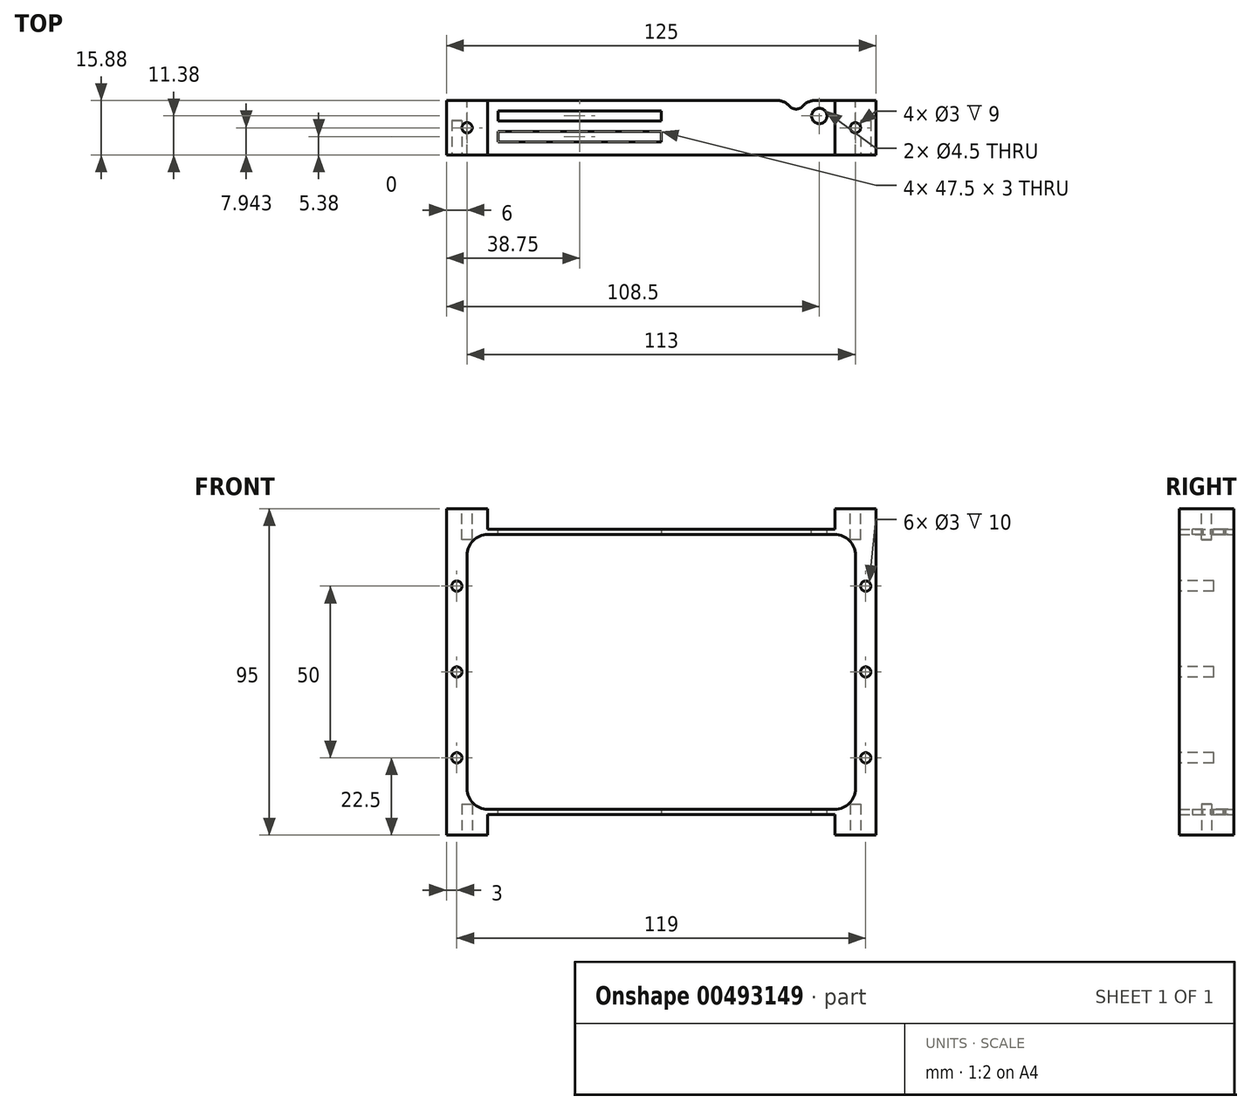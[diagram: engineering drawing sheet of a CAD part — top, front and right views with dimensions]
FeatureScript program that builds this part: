
annotation { "Feature Type Name" : "Feature", "Feature Type Description" : "" }
export const myFeature = defineFeature(function(context is Context, id is Id, definition is map)
    precondition{}
    {
        {
            var Q0;
            Q0=qCreatedBy(makeId("Front.planeOp"),FACE);
            var sketch = newSketch(context, id + "F0", { "sketchPlane" : qUnion([Q0])});
            skLineSegment(sketch, "E0.bottom", {"start": v(62.5, 47.5) * mm, "end": v(-62.5, 47.5) * mm, "construction": true});
            skLineSegment(sketch, "E0.top", {"start": v(62.5, -47.5) * mm, "end": v(-62.5, -47.5) * mm, "construction": true});
            skLineSegment(sketch, "E0.left", {"start": v(62.5, 47.5) * mm, "end": v(62.5, -47.5) * mm, "construction": true});
            skLineSegment(sketch, "E0.right", {"start": v(-62.5, 47.5) * mm, "end": v(-62.5, -47.5) * mm, "construction": true});
            skPoint(sketch, "E0.middle", {"position": v(0, 0) * mm});
            skLineSegment(sketch, "E1", {"start": v(-62.5, 47.5) * mm, "end": v(-50.5, 47.5) * mm});
            skLineSegment(sketch, "E2", {"start": v(62.5, 47.5) * mm, "end": v(50.5, 47.5) * mm});
            skLineSegment(sketch, "E3", {"start": v(50.5, 47.5) * mm, "end": v(50.5, 41.5) * mm});
            skLineSegment(sketch, "E4", {"start": v(50.5, 41.5) * mm, "end": v(-50.5, 41.5) * mm});
            skLineSegment(sketch, "E5", {"start": v(-50.5, 41.5) * mm, "end": v(-50.5, 47.5) * mm});
            skLineSegment(sketch, "E6", {"start": v(62.5, 47.5) * mm, "end": v(62.5, -47.5) * mm});
            skLineSegment(sketch, "E7", {"start": v(-62.5, -47.5) * mm, "end": v(-62.5, 47.5) * mm});
            skLineSegment(sketch, "E8", {"start": v(62.5, -47.5) * mm, "end": v(50.5, -47.5) * mm});
            skLineSegment(sketch, "E9", {"start": v(50.5, -47.5) * mm, "end": v(50.5, -41.5) * mm});
            skLineSegment(sketch, "E10", {"start": v(50.5, -41.5) * mm, "end": v(-50.5, -41.5) * mm});
            skLineSegment(sketch, "E11", {"start": v(-50.5, -41.5) * mm, "end": v(-50.5, -47.5) * mm});
            skLineSegment(sketch, "E12", {"start": v(-50.5, -47.5) * mm, "end": v(-62.5, -47.5) * mm});
            skLineSegment(sketch, "E13.bottom", {"start": v(56.5, 40) * mm, "end": v(-56.5, 40) * mm, "construction": true});
            skLineSegment(sketch, "E13.top", {"start": v(56.5, -40) * mm, "end": v(-56.5, -40) * mm, "construction": true});
            skLineSegment(sketch, "E13.left", {"start": v(56.5, 40) * mm, "end": v(56.5, -40) * mm, "construction": true});
            skLineSegment(sketch, "E13.right", {"start": v(-56.5, 40) * mm, "end": v(-56.5, -40) * mm, "construction": true});
            skLineSegment(sketch, "E14.bottom", {"start": v(56.5, 40) * mm, "end": v(-56.5, 40) * mm});
            skLineSegment(sketch, "E14.top", {"start": v(56.5, -40) * mm, "end": v(-56.5, -40) * mm});
            skLineSegment(sketch, "E14.left", {"start": v(56.5, 40) * mm, "end": v(56.5, -40) * mm});
            skLineSegment(sketch, "E14.right", {"start": v(-56.5, 40) * mm, "end": v(-56.5, -40) * mm});
            skSolve(sketch);
        }
        {
            var Q0;
            Q0 = qSketchRegion(id + "F0", true);
            extrude(context, id + "F1", {"entities" : qUnion([Q0]), "depth" : 15.88 * mm});
        }
        {
            var Q0;
            Q0=makeQuery(id+"F1.opExtrude","SWEPT_EDGE",EDGE,{"disambiguationData":[OSD([sQuery(id+"F0.wireOp",EDGE,"E14.bottom"),sQuery(id+"F0.wireOp",EDGE,"E14.left")])]});
            var Q1;
            Q1=makeQuery(id+"F1.opExtrude","SWEPT_EDGE",EDGE,{"disambiguationData":[OSD([sQuery(id+"F0.wireOp",EDGE,"E14.top"),sQuery(id+"F0.wireOp",EDGE,"E14.left")])]});
            var Q2;
            Q2=makeQuery(id+"F1.opExtrude","SWEPT_EDGE",EDGE,{"disambiguationData":[OSD([sQuery(id+"F0.wireOp",EDGE,"E14.top"),sQuery(id+"F0.wireOp",EDGE,"E14.right")])]});
            var Q3;
            Q3=makeQuery(id+"F1.opExtrude","SWEPT_EDGE",EDGE,{"disambiguationData":[OSD([sQuery(id+"F0.wireOp",EDGE,"E14.bottom"),sQuery(id+"F0.wireOp",EDGE,"E14.right")])]});
            fillet(context, id + "F2", {"entities" : qUnion([Q0, Q1, Q2, Q3]), "radius" : 6 * mm, "tangentPropagation" : true, "allowEdgeOverflow" : false});
        }
        {
            var Q0;
            Q0=makeQuery(id+"F1.opExtrude","SWEPT_FACE",FACE,{"disambiguationData":[OSD([sQuery(id+"F0.wireOp",EDGE,"E4")])]});
            var sketch = newSketch(context, id + "F3", { "sketchPlane" : qUnion([Q0])});
            skLineSegment(sketch, "E15.bottom", {"start": v(-47.5, -3) * mm, "end": v(41.5, -3) * mm});
            skLineSegment(sketch, "E15.top", {"start": v(-47.5, -6) * mm, "end": v(41.5, -6) * mm});
            skLineSegment(sketch, "E15.left", {"start": v(-47.5, -3) * mm, "end": v(-47.5, -6) * mm});
            skLineSegment(sketch, "E15.right", {"start": v(41.5, -3) * mm, "end": v(41.5, -6) * mm});
            skLineSegment(sketch, "E16.bottom", {"start": v(-47.5, -9) * mm, "end": v(47.5, -9) * mm});
            skLineSegment(sketch, "E16.top", {"start": v(-47.5, -12) * mm, "end": v(47.5, -12) * mm});
            skLineSegment(sketch, "E16.left", {"start": v(-47.5, -9) * mm, "end": v(-47.5, -12) * mm});
            skLineSegment(sketch, "E16.right", {"start": v(47.5, -9) * mm, "end": v(47.5, -12) * mm});
            skCircle(sketch, "E17", {"center": v(46, -4.5) * mm, "radius": 1.5 * mm});
            skSolve(sketch);
        }
        {
            var Q0;
            Q0 = qSketchRegion(id + "F3", true);
            extrude(context, id + "F4", {"entities" : qUnion([Q0]), "operationType" : NewBodyOperationType.REMOVE, "oppositeDirection" : true, "depth" : 132 * mm});
        }
        {
            var Q0;
            Q0=makeQuery(id+"F1.opExtrude","CAP_FACE",FACE,{"disambiguationData":[OSD([sQuery(id+"F0.wireOp",EDGE,"E1"),sQuery(id+"F0.wireOp",EDGE,"E2"),sQuery(id+"F0.wireOp",EDGE,"E3"),sQuery(id+"F0.wireOp",EDGE,"E4"),sQuery(id+"F0.wireOp",EDGE,"E5"),sQuery(id+"F0.wireOp",EDGE,"E6"),sQuery(id+"F0.wireOp",EDGE,"E7"),sQuery(id+"F0.wireOp",EDGE,"E8"),sQuery(id+"F0.wireOp",EDGE,"E9"),sQuery(id+"F0.wireOp",EDGE,"E10"),sQuery(id+"F0.wireOp",EDGE,"E11"),sQuery(id+"F0.wireOp",EDGE,"E12"),sQuery(id+"F0.wireOp",EDGE,"E14.bottom"),sQuery(id+"F0.wireOp",EDGE,"E14.top"),sQuery(id+"F0.wireOp",EDGE,"E14.left"),sQuery(id+"F0.wireOp",EDGE,"E14.right")])],"isStart":false});
            var sketch = newSketch(context, id + "F5", { "sketchPlane" : qUnion([Q0])});
            skLineSegment(sketch, "E18.bottom", {"start": v(-62.5, 32.98) * mm, "end": v(-56.5, 32.98) * mm, "construction": true});
            skLineSegment(sketch, "E18.top", {"start": v(-62.5, -31.1) * mm, "end": v(-56.5, -31.1) * mm, "construction": true});
            skLineSegment(sketch, "E18.left", {"start": v(-62.5, 32.98) * mm, "end": v(-62.5, -31.1) * mm, "construction": true});
            skLineSegment(sketch, "E18.right", {"start": v(-56.5, 32.98) * mm, "end": v(-56.5, -31.1) * mm, "construction": true});
            skLineSegment(sketch, "E19.bottom", {"start": v(56.5, 34) * mm, "end": v(62.5, 34) * mm, "construction": true});
            skLineSegment(sketch, "E19.top", {"start": v(56.5, -34) * mm, "end": v(62.5, -34) * mm, "construction": true});
            skLineSegment(sketch, "E19.left", {"start": v(56.5, 34) * mm, "end": v(56.5, -34) * mm, "construction": true});
            skLineSegment(sketch, "E19.right", {"start": v(62.5, 34) * mm, "end": v(62.5, -34) * mm, "construction": true});
            skLineSegment(sketch, "E20", {"start": v(-59.5, 32.98) * mm, "end": v(-59.5, -31.1) * mm, "construction": true});
            skLineSegment(sketch, "E21", {"start": v(-59.5, -31.1) * mm, "end": v(59.5, -34) * mm, "construction": true});
            skLineSegment(sketch, "E22", {"start": v(59.5, -34) * mm, "end": v(59.5, 34) * mm, "construction": true});
            skCircle(sketch, "E23", {"center": v(-59.5, 0) * mm, "radius": 1.5 * mm});
            skPoint(sketch, "E23.centerSnap0", {"position": v(-56.5, 0) * mm});
            skCircle(sketch, "E24", {"center": v(59.5, 0) * mm, "radius": 1.5 * mm});
            skCircle(sketch, "E25", {"center": v(59.5, -25) * mm, "radius": 1.5 * mm});
            skCircle(sketch, "E26", {"center": v(59.5, 25) * mm, "radius": 1.5 * mm});
            skCircle(sketch, "E27", {"center": v(-59.5, 25) * mm, "radius": 1.5 * mm});
            skCircle(sketch, "E28", {"center": v(-59.5, -25) * mm, "radius": 1.5 * mm});
            skSolve(sketch);
        }
        {
            var Q0;
            Q0 = qSketchRegion(id + "F5", true);
            extrude(context, id + "F6", {"entities" : qUnion([Q0]), "operationType" : NewBodyOperationType.REMOVE, "oppositeDirection" : true, "depth" : 10 * mm});
        }
        {
            var Q0;
            Q0=makeQuery(id+"F1.opExtrude","SWEPT_FACE",FACE,{"disambiguationData":[OSD([sQuery(id+"F0.wireOp",EDGE,"E4")])]});
            var sketch = newSketch(context, id + "F7", { "sketchPlane" : qUnion([Q0])});
            skLineSegment(sketch, "E29.bottom", {"start": v(0, 0) * mm, "end": v(42.94, 0) * mm});
            skLineSegment(sketch, "E29.top", {"start": v(0, -7.4) * mm, "end": v(42.94, -7.4) * mm});
            skLineSegment(sketch, "E29.left", {"start": v(0, 0) * mm, "end": v(0, -7.4) * mm});
            skLineSegment(sketch, "E29.right", {"start": v(42.94, 0) * mm, "end": v(42.94, -7.4) * mm});
            skLineSegment(sketch, "E30.bottom", {"start": v(0, -7.4) * mm, "end": v(49.14, -7.4) * mm});
            skLineSegment(sketch, "E30.top", {"start": v(0, -14.14) * mm, "end": v(49.14, -14.14) * mm});
            skLineSegment(sketch, "E30.left", {"start": v(0, -7.4) * mm, "end": v(0, -14.14) * mm});
            skLineSegment(sketch, "E30.right", {"start": v(49.14, -7.4) * mm, "end": v(49.14, -14.14) * mm});
            skSolve(sketch);
        }
        {
            var Q0;
            Q0 = qSketchRegion(id + "F7", true);
            extrude(context, id + "F8", {"entities" : qUnion([Q0]), "operationType" : NewBodyOperationType.ADD, "oppositeDirection" : true, "depth" : 1.5 * mm});
        }
        {
            var Q0;
            Q0=makeQuery(id+"F1.opExtrude","SWEPT_FACE",FACE,{"disambiguationData":[OSD([sQuery(id+"F0.wireOp",EDGE,"E10")])]});
            var sketch = newSketch(context, id + "F9", { "sketchPlane" : qUnion([Q0])});
            skLineSegment(sketch, "E31.bottom", {"start": v(0, 15.88) * mm, "end": v(49.01, 15.88) * mm});
            skLineSegment(sketch, "E31.top", {"start": v(0, 7.24) * mm, "end": v(49.01, 7.24) * mm});
            skLineSegment(sketch, "E31.left", {"start": v(0, 15.88) * mm, "end": v(0, 7.24) * mm});
            skLineSegment(sketch, "E31.right", {"start": v(49.01, 15.88) * mm, "end": v(49.01, 7.24) * mm});
            skLineSegment(sketch, "E32.bottom", {"start": v(0, 0) * mm, "end": v(42.8, 0) * mm});
            skLineSegment(sketch, "E32.top", {"start": v(0, 7.24) * mm, "end": v(42.8, 7.24) * mm});
            skLineSegment(sketch, "E32.left", {"start": v(0, 0) * mm, "end": v(0, 7.24) * mm});
            skLineSegment(sketch, "E32.right", {"start": v(42.8, 0) * mm, "end": v(42.8, 7.24) * mm});
            skSolve(sketch);
        }
        {
            var Q0;
            Q0 = qSketchRegion(id + "F9", true);
            extrude(context, id + "F10", {"entities" : qUnion([Q0]), "operationType" : NewBodyOperationType.ADD, "oppositeDirection" : true, "depth" : 1.5 * mm});
        }
        {
            var Q0;
            Q0=makeQuery(id+"F8.boolean.opBoolean","MERGE",FACE,{"derivedFrom":[makeQuery(id+"F1.opExtrude","SWEPT_FACE",FACE,{"disambiguationData":[OSD([sQuery(id+"F0.wireOp",EDGE,"E4")])]}),makeQuery(id+"F8.opExtrude","CAP_FACE",FACE,{"disambiguationData":[OSD([sQuery(id+"F7.wireOp",EDGE,"E29.bottom"),sQuery(id+"F7.wireOp",EDGE,"E29.left"),sQuery(id+"F7.wireOp",EDGE,"E29.right"),sQuery(id+"F7.wireOp",EDGE,"E30.bottom"),sQuery(id+"F7.wireOp",EDGE,"E30.top"),sQuery(id+"F7.wireOp",EDGE,"E30.left"),sQuery(id+"F7.wireOp",EDGE,"E30.right")])],"isStart":true})]});
            var sketch = newSketch(context, id + "F11", { "sketchPlane" : qUnion([Q0])});
            skCircle(sketch, "E33", {"center": v(39.25, 0) * mm, "radius": 2.5 * mm});
            skSolve(sketch);
        }
        {
            var Q0;
            Q0 = qSketchRegion(id + "F11", true);
            extrude(context, id + "F12", {"entities" : qUnion([Q0]), "operationType" : NewBodyOperationType.REMOVE, "oppositeDirection" : true, "depth" : 92 * mm});
        }
        {
            var Q0;
            Q0=makeQuery(id+"F8.boolean.opBoolean","MERGE",FACE,{"derivedFrom":[makeQuery(id+"F1.opExtrude","SWEPT_FACE",FACE,{"disambiguationData":[OSD([sQuery(id+"F0.wireOp",EDGE,"E4")])]}),makeQuery(id+"F8.opExtrude","CAP_FACE",FACE,{"disambiguationData":[OSD([sQuery(id+"F7.wireOp",EDGE,"E29.bottom"),sQuery(id+"F7.wireOp",EDGE,"E29.left"),sQuery(id+"F7.wireOp",EDGE,"E29.right"),sQuery(id+"F7.wireOp",EDGE,"E30.bottom"),sQuery(id+"F7.wireOp",EDGE,"E30.top"),sQuery(id+"F7.wireOp",EDGE,"E30.left"),sQuery(id+"F7.wireOp",EDGE,"E30.right")])],"isStart":true})]});
            var sketch = newSketch(context, id + "F13", { "sketchPlane" : qUnion([Q0])});
            skCircle(sketch, "E34", {"center": v(46, -4.5) * mm, "radius": 2.25 * mm});
            skSolve(sketch);
        }
        {
            var Q0;
            Q0 = qSketchRegion(id + "F13", true);
            extrude(context, id + "F14", {"entities" : qUnion([Q0]), "operationType" : NewBodyOperationType.REMOVE, "oppositeDirection" : true, "depth" : 200 * mm});
        }
        {
            var Q0;
            Q0=makeQuery(id+"F12.boolean.opBoolean","INTERSECT",EDGE,{"disambiguationData":[OD(2.0)],"derivedFrom":[makeQuery(id+"F1.opExtrude","CAP_FACE",FACE,{"disambiguationData":[OSD([sQuery(id+"F0.wireOp",EDGE,"E1"),sQuery(id+"F0.wireOp",EDGE,"E2"),sQuery(id+"F0.wireOp",EDGE,"E3"),sQuery(id+"F0.wireOp",EDGE,"E4"),sQuery(id+"F0.wireOp",EDGE,"E5"),sQuery(id+"F0.wireOp",EDGE,"E6"),sQuery(id+"F0.wireOp",EDGE,"E7"),sQuery(id+"F0.wireOp",EDGE,"E8"),sQuery(id+"F0.wireOp",EDGE,"E9"),sQuery(id+"F0.wireOp",EDGE,"E10"),sQuery(id+"F0.wireOp",EDGE,"E11"),sQuery(id+"F0.wireOp",EDGE,"E12"),sQuery(id+"F0.wireOp",EDGE,"E14.bottom"),sQuery(id+"F0.wireOp",EDGE,"E14.top"),sQuery(id+"F0.wireOp",EDGE,"E14.left"),sQuery(id+"F0.wireOp",EDGE,"E14.right")])],"isStart":true}),makeQuery(id+"F12.opExtrude","SWEPT_FACE",FACE,{"disambiguationData":[OSD([sQuery(id+"F11.wireOp",EDGE,"E33")])]})]});
            var Q1;
            Q1=makeQuery(id+"F12.boolean.opBoolean","INTERSECT",EDGE,{"disambiguationData":[OD(3.0)],"derivedFrom":[makeQuery(id+"F1.opExtrude","CAP_FACE",FACE,{"disambiguationData":[OSD([sQuery(id+"F0.wireOp",EDGE,"E1"),sQuery(id+"F0.wireOp",EDGE,"E2"),sQuery(id+"F0.wireOp",EDGE,"E3"),sQuery(id+"F0.wireOp",EDGE,"E4"),sQuery(id+"F0.wireOp",EDGE,"E5"),sQuery(id+"F0.wireOp",EDGE,"E6"),sQuery(id+"F0.wireOp",EDGE,"E7"),sQuery(id+"F0.wireOp",EDGE,"E8"),sQuery(id+"F0.wireOp",EDGE,"E9"),sQuery(id+"F0.wireOp",EDGE,"E10"),sQuery(id+"F0.wireOp",EDGE,"E11"),sQuery(id+"F0.wireOp",EDGE,"E12"),sQuery(id+"F0.wireOp",EDGE,"E14.bottom"),sQuery(id+"F0.wireOp",EDGE,"E14.top"),sQuery(id+"F0.wireOp",EDGE,"E14.left"),sQuery(id+"F0.wireOp",EDGE,"E14.right")])],"isStart":true}),makeQuery(id+"F12.opExtrude","SWEPT_FACE",FACE,{"disambiguationData":[OSD([sQuery(id+"F11.wireOp",EDGE,"E33")])]})]});
            fillet(context, id + "F15", {"entities" : qUnion([Q0, Q1]), "radius" : 5 * mm, "tangentPropagation" : true, "allowEdgeOverflow" : false});
        }
        {
            var Q0;
            Q0=makeQuery(id+"F1.opExtrude","SWEPT_FACE",FACE,{"disambiguationData":[OSD([sQuery(id+"F0.wireOp",EDGE,"E1")])]});
            var sketch = newSketch(context, id + "F16", { "sketchPlane" : qUnion([Q0])});
            skLineSegment(sketch, "E35", {"start": v(-62.5, 0) * mm, "end": v(-50.5, -15.88) * mm, "construction": true});
            skCircle(sketch, "E36", {"center": v(-56.5, -7.94) * mm, "radius": 1.5 * mm});
            skSolve(sketch);
        }
        {
            var Q0;
            Q0 = qSketchRegion(id + "F16", true);
            extrude(context, id + "F17", {"entities" : qUnion([Q0]), "operationType" : NewBodyOperationType.REMOVE, "oppositeDirection" : true, "depth" : 9 * mm});
        }
        {
            var Q0;
            Q0=makeQuery(id+"F1.opExtrude","SWEPT_FACE",FACE,{"disambiguationData":[OSD([sQuery(id+"F0.wireOp",EDGE,"E2")])]});
            var sketch = newSketch(context, id + "F18", { "sketchPlane" : qUnion([Q0])});
            skLineSegment(sketch, "E37", {"start": v(62.5, 0) * mm, "end": v(50.5, -15.88) * mm, "construction": true});
            skCircle(sketch, "E38", {"center": v(56.5, -7.94) * mm, "radius": 1.5 * mm});
            skSolve(sketch);
        }
        {
            var Q0;
            Q0 = qSketchRegion(id + "F18", true);
            extrude(context, id + "F19", {"entities" : qUnion([Q0]), "operationType" : NewBodyOperationType.REMOVE, "oppositeDirection" : true, "depth" : 9 * mm});
        }
        {
            var Q0;
            Q0=makeQuery(id+"F1.opExtrude","SWEPT_FACE",FACE,{"disambiguationData":[OSD([sQuery(id+"F0.wireOp",EDGE,"E12")])]});
            var sketch = newSketch(context, id + "F20", { "sketchPlane" : qUnion([Q0])});
            skLineSegment(sketch, "E39", {"start": v(-62.5, 15.88) * mm, "end": v(-50.5, 0) * mm, "construction": true});
            skCircle(sketch, "E40", {"center": v(-56.5, 7.94) * mm, "radius": 1.5 * mm});
            skSolve(sketch);
        }
        {
            var Q0;
            Q0 = qSketchRegion(id + "F20", true);
            extrude(context, id + "F21", {"entities" : qUnion([Q0]), "operationType" : NewBodyOperationType.REMOVE, "oppositeDirection" : true, "depth" : 9 * mm});
        }
        {
            var Q0;
            Q0=makeQuery(id+"F1.opExtrude","SWEPT_FACE",FACE,{"disambiguationData":[OSD([sQuery(id+"F0.wireOp",EDGE,"E8")])]});
            var sketch = newSketch(context, id + "F22", { "sketchPlane" : qUnion([Q0])});
            skLineSegment(sketch, "E41", {"start": v(62.5, 15.88) * mm, "end": v(50.5, 0) * mm, "construction": true});
            skCircle(sketch, "E42", {"center": v(56.5, 7.94) * mm, "radius": 1.5 * mm});
            skSolve(sketch);
        }
        {
            var Q0;
            Q0 = qSketchRegion(id + "F22", true);
            extrude(context, id + "F23", {"entities" : qUnion([Q0]), "operationType" : NewBodyOperationType.REMOVE, "oppositeDirection" : true, "depth" : 9 * mm});
        }
    });
